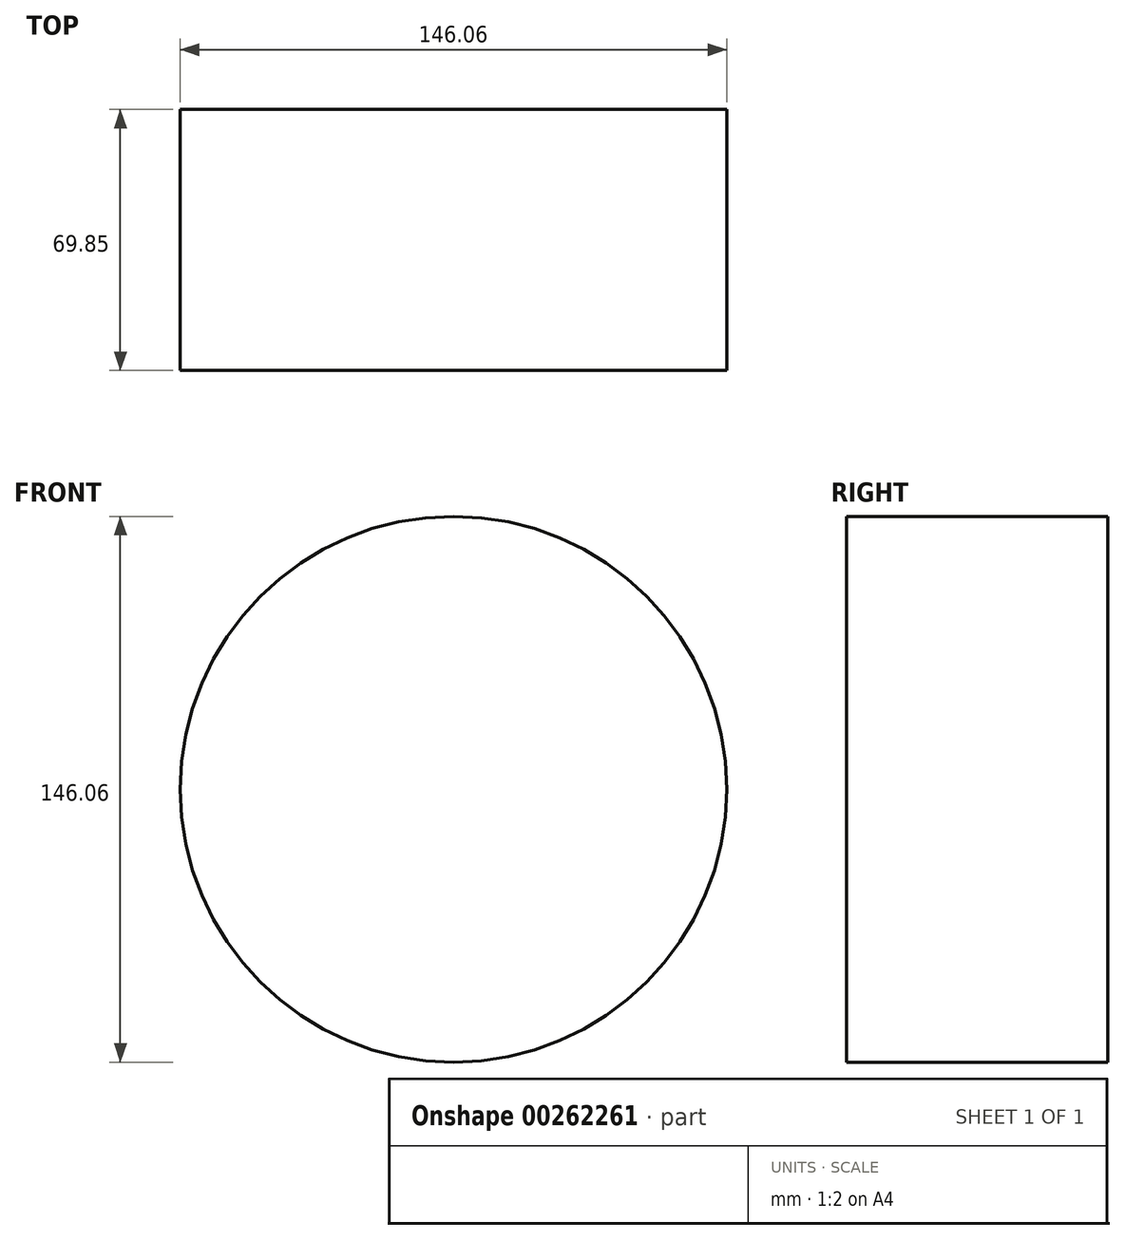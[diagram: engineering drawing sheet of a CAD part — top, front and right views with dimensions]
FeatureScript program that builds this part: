
annotation { "Feature Type Name" : "Feature", "Feature Type Description" : "" }
export const myFeature = defineFeature(function(context is Context, id is Id, definition is map)
    precondition{}
    {
        {
            var Q0;
            Q0=qCreatedBy(makeId("Front.planeOp"),FACE);
            var sketch = newSketch(context, id + "F0", { "sketchPlane" : qUnion([Q0])});
            skCircle(sketch, "E0", {"center": v(0, 0) * mm, "radius": 73.03 * mm});
            skSolve(sketch);
        }
        {
            var Q0;
            Q0=makeQuery(id+"F0.imprint","IMPRINT",FACE,{"disambiguationData":[TD([[makeQuery(id+"F0.imprint","IMPRINT",EDGE,{"derivedFrom":sQuery(id+"F0.wireOp",EDGE,"E0")}),1.0]])]});
            extrude(context, id + "F1", {"entities" : qUnion([Q0]), "depth" : 69.85 * mm});
        }
    });
